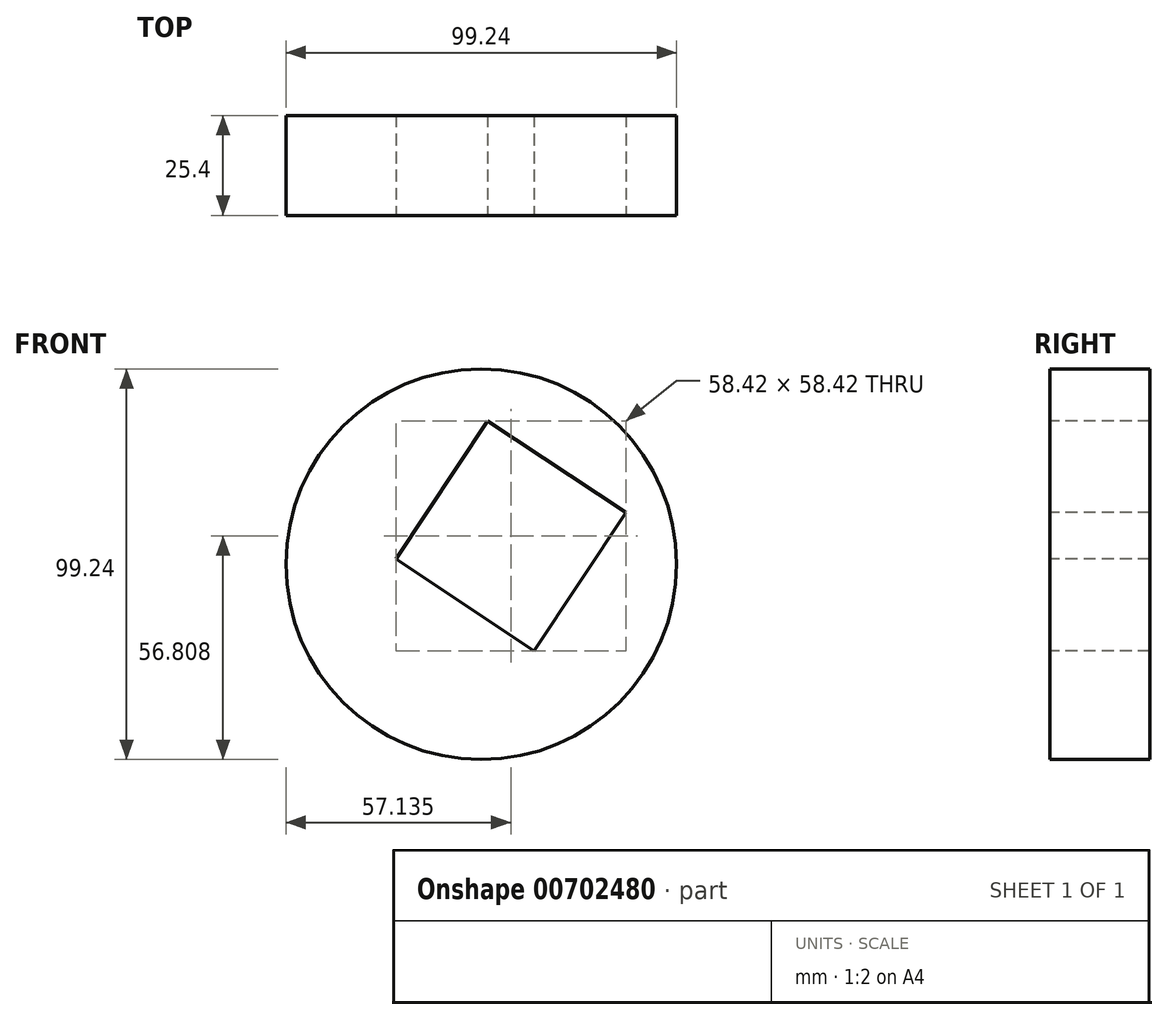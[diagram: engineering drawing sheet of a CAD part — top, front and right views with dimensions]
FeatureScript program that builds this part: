
annotation { "Feature Type Name" : "Feature", "Feature Type Description" : "" }
export const myFeature = defineFeature(function(context is Context, id is Id, definition is map)
    precondition{}
    {
        {
            var Q0;
            Q0=qCreatedBy(makeId("Front.planeOp"),FACE);
            var sketch = newSketch(context, id + "F0", { "sketchPlane" : qUnion([Q0])});
            skCircle(sketch, "E0", {"center": v(4.14, 0) * mm, "radius": 49.62 * mm});
            skSolve(sketch);
        }
        {
            var Q0;
            Q0=makeQuery(id+"F0.imprint","IMPRINT",FACE,{"disambiguationData":[TD([[makeQuery(id+"F0.imprint","IMPRINT",EDGE,{"derivedFrom":sQuery(id+"F0.wireOp",EDGE,"E0")}),1.0]])]});
            extrude(context, id + "F1", {"entities" : qUnion([Q0]), "depth" : 25.4 * mm, "offsetDistance" : 25.4 * mm});
        }
        {
            var Q0;
            Q0=makeQuery(id+"F1.opExtrude","CAP_FACE",FACE,{"disambiguationData":[OSD([sQuery(id+"F0.wireOp",EDGE,"E0")])],"isStart":false});
            var sketch = newSketch(context, id + "F2", { "sketchPlane" : qUnion([Q0])});
            skCircle(sketch, "E1.cCircle", {"center": v(11.66, 7.19) * mm, "radius": 21.07 * mm, "construction": true});
            skLineSegment(sketch, "E1.0", {"start": v(17.56, -22.02) * mm, "end": v(-17.56, 1.29) * mm});
            skLineSegment(sketch, "E1.1", {"start": v(-17.56, 1.29) * mm, "end": v(5.76, 36.4) * mm});
            skLineSegment(sketch, "E1.2", {"start": v(5.76, 36.4) * mm, "end": v(40.87, 13.09) * mm});
            skLineSegment(sketch, "E1.3", {"start": v(40.87, 13.09) * mm, "end": v(17.56, -22.02) * mm});
            skPoint(sketch, "E1.0.midPoint", {"position": v(0, -10.37) * mm});
            skSolve(sketch);
        }
        {
            var Q0;
            Q0 = qSketchRegion(id + "F2", true);
            extrude(context, id + "F3", {"entities" : qUnion([Q0]), "operationType" : NewBodyOperationType.REMOVE, "endBound" : BoundingType.UP_TO_NEXT, "oppositeDirection" : true, "depth" : 25 * mm, "offsetDistance" : 25 * mm});
        }
    });
